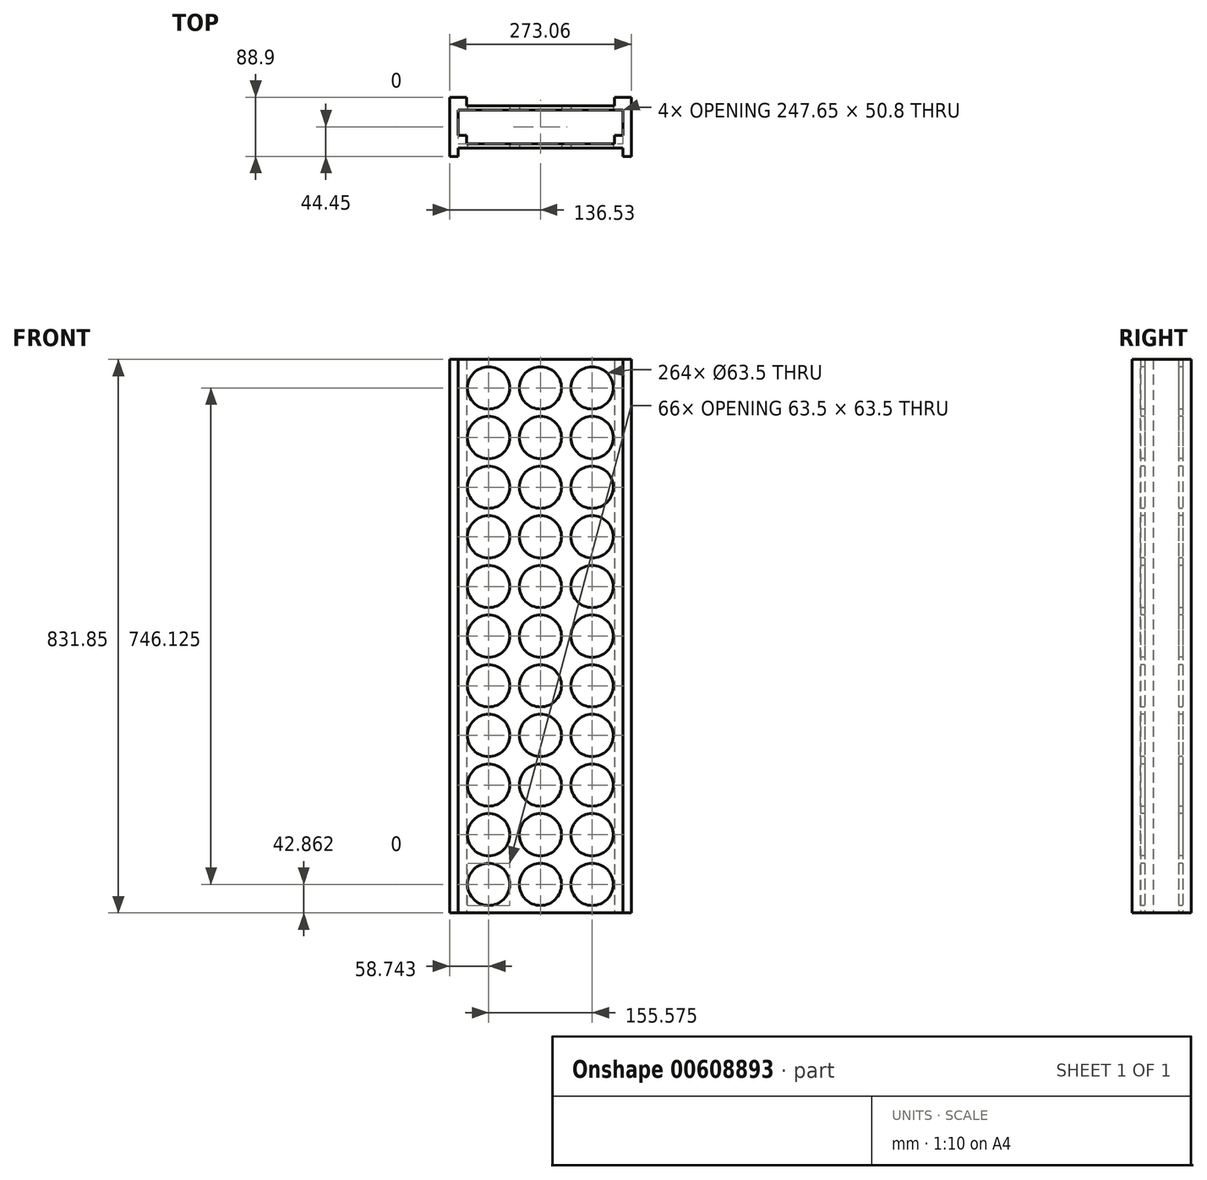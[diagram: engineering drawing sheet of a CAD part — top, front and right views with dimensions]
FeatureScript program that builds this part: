
annotation { "Feature Type Name" : "Feature", "Feature Type Description" : "" }
export const myFeature = defineFeature(function(context is Context, id is Id, definition is map)
    precondition{}
    {
        {
            var Q0;
            Q0=qCreatedBy(makeId("Top.planeOp"),FACE);
            var sketch = newSketch(context, id + "F0", { "sketchPlane" : qUnion([Q0])});
            skLineSegment(sketch, "E0", {"start": v(0, 0) * mm, "end": v(136.52, 0) * mm, "construction": true});
            skLineSegment(sketch, "E1", {"start": v(0, 0) * mm, "end": v(-136.53, 0) * mm, "construction": true});
            skLineSegment(sketch, "E2", {"start": v(-136.53, 0) * mm, "end": v(-136.53, 44.45) * mm, "construction": true});
            skLineSegment(sketch, "E3", {"start": v(-136.53, 0) * mm, "end": v(-136.53, -44.45) * mm, "construction": true});
            skLineSegment(sketch, "E4", {"start": v(136.52, 0) * mm, "end": v(136.52, 44.45) * mm, "construction": true});
            skLineSegment(sketch, "E5", {"start": v(136.52, 0) * mm, "end": v(136.52, -44.45) * mm, "construction": true});
            skLineSegment(sketch, "E6.bottom", {"start": v(-136.53, 44.45) * mm, "end": v(-123.83, 44.45) * mm});
            skLineSegment(sketch, "E6.top", {"start": v(-136.53, -44.45) * mm, "end": v(-123.83, -44.45) * mm});
            skLineSegment(sketch, "E6.left", {"start": v(-136.53, 44.45) * mm, "end": v(-136.53, -44.45) * mm});
            skLineSegment(sketch, "E6.right", {"start": v(-123.83, 44.45) * mm, "end": v(-123.83, -44.45) * mm});
            skLineSegment(sketch, "E7.bottom", {"start": v(136.52, 44.45) * mm, "end": v(123.82, 44.45) * mm});
            skLineSegment(sketch, "E7.top", {"start": v(136.52, -44.45) * mm, "end": v(123.83, -44.45) * mm});
            skLineSegment(sketch, "E7.left", {"start": v(136.52, 44.45) * mm, "end": v(136.52, -44.45) * mm});
            skLineSegment(sketch, "E7.right", {"start": v(123.82, 44.45) * mm, "end": v(123.83, -44.45) * mm});
            skLineSegment(sketch, "E8", {"start": v(-123.83, -44.45) * mm, "end": v(-123.83, -31.75) * mm, "construction": true});
            skLineSegment(sketch, "E9.left", {"start": v(-123.83, -31.75) * mm, "end": v(-123.83, -25.4) * mm});
            skLineSegment(sketch, "E9.right", {"start": v(123.83, -31.75) * mm, "end": v(123.83, -25.4) * mm});
            skLineSegment(sketch, "E10.bottom", {"start": v(-123.83, -31.75) * mm, "end": v(123.83, -31.75) * mm});
            skLineSegment(sketch, "E10.top", {"start": v(-123.83, -25.4) * mm, "end": v(123.83, -25.4) * mm});
            skLineSegment(sketch, "E11.bottom", {"start": v(-123.83, -25.4) * mm, "end": v(-111.12, -25.4) * mm});
            skLineSegment(sketch, "E11.top", {"start": v(-123.83, -12.7) * mm, "end": v(-111.12, -12.7) * mm});
            skLineSegment(sketch, "E11.left", {"start": v(-123.83, -25.4) * mm, "end": v(-123.83, -12.7) * mm});
            skLineSegment(sketch, "E11.right", {"start": v(-111.12, -25.4) * mm, "end": v(-111.12, -12.7) * mm});
            skLineSegment(sketch, "E12.bottom", {"start": v(123.83, -25.4) * mm, "end": v(111.12, -25.4) * mm});
            skLineSegment(sketch, "E12.top", {"start": v(123.83, -12.7) * mm, "end": v(111.12, -12.7) * mm});
            skLineSegment(sketch, "E12.left", {"start": v(123.83, -25.4) * mm, "end": v(123.83, -12.7) * mm});
            skLineSegment(sketch, "E12.right", {"start": v(111.12, -25.4) * mm, "end": v(111.12, -12.7) * mm});
            skLineSegment(sketch, "E13.bottom", {"start": v(-123.83, 44.45) * mm, "end": v(-111.12, 44.45) * mm});
            skLineSegment(sketch, "E13.top", {"start": v(-123.83, 31.75) * mm, "end": v(-111.12, 31.75) * mm});
            skLineSegment(sketch, "E13.left", {"start": v(-123.83, 44.45) * mm, "end": v(-123.83, 31.75) * mm});
            skLineSegment(sketch, "E13.right", {"start": v(-111.12, 44.45) * mm, "end": v(-111.12, 31.75) * mm});
            skLineSegment(sketch, "E14.bottom", {"start": v(123.82, 44.45) * mm, "end": v(111.12, 44.45) * mm});
            skLineSegment(sketch, "E14.top", {"start": v(123.82, 31.75) * mm, "end": v(111.12, 31.75) * mm});
            skLineSegment(sketch, "E14.left", {"start": v(123.82, 44.45) * mm, "end": v(123.82, 31.75) * mm});
            skLineSegment(sketch, "E14.right", {"start": v(111.12, 44.45) * mm, "end": v(111.12, 31.75) * mm});
            skLineSegment(sketch, "E15.bottom", {"start": v(-123.82, 31.75) * mm, "end": v(123.82, 31.75) * mm});
            skLineSegment(sketch, "E15.top", {"start": v(-123.82, 25.4) * mm, "end": v(123.82, 25.4) * mm});
            skLineSegment(sketch, "E15.left", {"start": v(-123.83, 31.75) * mm, "end": v(-123.83, 25.4) * mm});
            skLineSegment(sketch, "E15.right", {"start": v(123.82, 31.75) * mm, "end": v(123.82, 25.4) * mm});
            skSolve(sketch);
        }
        {
            var Q0;
            {var subQ4=sQuery(id+"F0.wireOp",EDGE,"E6.bottom");Q0=makeQuery(id+"F0.imprint","IMPRINT",FACE,{"disambiguationData":[TD([[makeQuery(id+"F0.imprint","IMPRINT",EDGE,{"derivedFrom":subQ4}),-1.0]])]});}
            var Q1;
            {var subQ0=sQuery(id+"F0.wireOp",EDGE,"E13.bottom");Q1=makeQuery(id+"F0.imprint","IMPRINT",FACE,{"disambiguationData":[TD([[makeQuery(id+"F0.imprint","IMPRINT",EDGE,{"derivedFrom":subQ0}),-1.0]])]});}
            var Q2;
            {var subQ3=sQuery(id+"F0.wireOp",EDGE,"E13.top");Q2=makeQuery(id+"F0.imprint","IMPRINT",FACE,{"disambiguationData":[TD([[makeQuery(id+"F0.imprint","IMPRINT",EDGE,{"derivedFrom":subQ3}),-1.0]])]});}
            var Q3;
            {var subQ0=sQuery(id+"F0.wireOp",EDGE,"E14.bottom");Q3=makeQuery(id+"F0.imprint","IMPRINT",FACE,{"disambiguationData":[TD([[makeQuery(id+"F0.imprint","IMPRINT",EDGE,{"derivedFrom":subQ0}),1.0]])]});}
            var Q4;
            {var subQ4=sQuery(id+"F0.wireOp",EDGE,"E7.bottom");Q4=makeQuery(id+"F0.imprint","IMPRINT",FACE,{"disambiguationData":[TD([[makeQuery(id+"F0.imprint","IMPRINT",EDGE,{"derivedFrom":subQ4}),1.0]])]});}
            var Q5;
            {var subQ0=sQuery(id+"F0.wireOp",EDGE,"E12.top");Q5=makeQuery(id+"F0.imprint","IMPRINT",FACE,{"disambiguationData":[TD([[makeQuery(id+"F0.imprint","IMPRINT",EDGE,{"derivedFrom":subQ0}),1.0]])]});}
            var Q6;
            {var subQ0=sQuery(id+"F0.wireOp",EDGE,"E11.top");Q6=makeQuery(id+"F0.imprint","IMPRINT",FACE,{"disambiguationData":[TD([[makeQuery(id+"F0.imprint","IMPRINT",EDGE,{"derivedFrom":subQ0}),-1.0]])]});}
            var Q7;
            {var subQ3=sQuery(id+"F0.wireOp",EDGE,"E10.bottom");Q7=makeQuery(id+"F0.imprint","IMPRINT",FACE,{"disambiguationData":[TD([[makeQuery(id+"F0.imprint","IMPRINT",EDGE,{"derivedFrom":subQ3}),1.0]])]});}
            extrude(context, id + "F1", {"entities" : qUnion([Q0, Q1, Q2, Q3, Q4, Q5, Q6, Q7]), "depth" : 831.85 * mm, "offsetDistance" : 25.4 * mm});
        }
        {
            var Q0;
            Q0=makeQuery(id+"F1.opExtrude","SWEPT_FACE",FACE,{"disambiguationData":[OSD([sQuery(id+"F0.wireOp",EDGE,"E10.bottom")])]});
            var sketch = newSketch(context, id + "F2", { "sketchPlane" : qUnion([Q0])});
            skLineSegment(sketch, "E16", {"start": v(-123.83, 0) * mm, "end": v(-123.83, 42.86) * mm, "construction": true});
            skLineSegment(sketch, "E17", {"start": v(-123.83, 42.86) * mm, "end": v(-123.83, 117.48) * mm, "construction": true});
            skLineSegment(sketch, "E18", {"start": v(-123.83, 117.48) * mm, "end": v(-123.83, 192.09) * mm, "construction": true});
            skLineSegment(sketch, "E19", {"start": v(-123.83, 192.09) * mm, "end": v(-123.83, 266.7) * mm, "construction": true});
            skLineSegment(sketch, "E20", {"start": v(-123.83, 266.7) * mm, "end": v(-123.83, 341.31) * mm, "construction": true});
            skLineSegment(sketch, "E21", {"start": v(-123.83, 341.31) * mm, "end": v(-123.83, 415.93) * mm, "construction": true});
            skLineSegment(sketch, "E22", {"start": v(-123.83, 415.93) * mm, "end": v(-123.83, 490.54) * mm, "construction": true});
            skLineSegment(sketch, "E23", {"start": v(-123.83, 490.54) * mm, "end": v(-123.83, 565.15) * mm, "construction": true});
            skLineSegment(sketch, "E24", {"start": v(-123.83, 565.15) * mm, "end": v(-123.83, 639.76) * mm, "construction": true});
            skLineSegment(sketch, "E25", {"start": v(-123.83, 639.76) * mm, "end": v(-123.83, 714.38) * mm, "construction": true});
            skLineSegment(sketch, "E26", {"start": v(-123.83, 714.38) * mm, "end": v(-123.83, 788.99) * mm, "construction": true});
            skLineSegment(sketch, "E27", {"start": v(-123.83, 788.99) * mm, "end": v(123.83, 788.99) * mm, "construction": true});
            skLineSegment(sketch, "E28", {"start": v(-123.83, 714.38) * mm, "end": v(123.83, 714.38) * mm, "construction": true});
            skLineSegment(sketch, "E29", {"start": v(123.83, 714.38) * mm, "end": v(123.9, 718.52) * mm, "construction": true});
            skLineSegment(sketch, "E30", {"start": v(-123.83, 639.76) * mm, "end": v(123.83, 639.76) * mm, "construction": true});
            skLineSegment(sketch, "E31", {"start": v(-123.83, 565.15) * mm, "end": v(123.83, 565.15) * mm, "construction": true});
            skLineSegment(sketch, "E32", {"start": v(-123.83, 490.54) * mm, "end": v(123.83, 490.54) * mm, "construction": true});
            skLineSegment(sketch, "E33", {"start": v(-123.83, 415.93) * mm, "end": v(123.83, 415.93) * mm, "construction": true});
            skLineSegment(sketch, "E34", {"start": v(123.83, 415.93) * mm, "end": v(120.66, 422.9) * mm, "construction": true});
            skLineSegment(sketch, "E35", {"start": v(-123.83, 341.31) * mm, "end": v(123.83, 341.31) * mm, "construction": true});
            skLineSegment(sketch, "E36", {"start": v(-123.83, 266.7) * mm, "end": v(123.83, 266.7) * mm, "construction": true});
            skLineSegment(sketch, "E37", {"start": v(-123.83, 192.09) * mm, "end": v(123.83, 192.09) * mm, "construction": true});
            skLineSegment(sketch, "E38", {"start": v(-123.83, 117.48) * mm, "end": v(123.83, 117.48) * mm, "construction": true});
            skLineSegment(sketch, "E39", {"start": v(-123.83, 42.86) * mm, "end": v(123.83, 42.86) * mm, "construction": true});
            skLineSegment(sketch, "E40", {"start": v(123.83, 0) * mm, "end": v(77.79, 0) * mm, "construction": true});
            skLineSegment(sketch, "E41", {"start": v(77.79, 0) * mm, "end": v(0, 0) * mm, "construction": true});
            skLineSegment(sketch, "E42", {"start": v(0, 0) * mm, "end": v(-77.79, 0) * mm, "construction": true});
            skLineSegment(sketch, "E43", {"start": v(-77.79, 0) * mm, "end": v(-77.79, 831.85) * mm, "construction": true});
            skLineSegment(sketch, "E44", {"start": v(0, 0) * mm, "end": v(0, 831.85) * mm, "construction": true});
            skLineSegment(sketch, "E45", {"start": v(77.79, 0) * mm, "end": v(77.79, 831.85) * mm, "construction": true});
            skLineSegment(sketch, "E46", {"start": v(77.79, 831.85) * mm, "end": v(76.8, 837.1) * mm, "construction": true});
            skCircle(sketch, "E47", {"center": v(-77.79, 42.86) * mm, "radius": 31.75 * mm});
            skCircle(sketch, "E48", {"center": v(-77.79, 117.48) * mm, "radius": 31.75 * mm});
            skCircle(sketch, "E49", {"center": v(-77.79, 192.09) * mm, "radius": 31.75 * mm});
            skCircle(sketch, "E50", {"center": v(-77.79, 266.7) * mm, "radius": 31.75 * mm});
            skCircle(sketch, "E51", {"center": v(0, 266.7) * mm, "radius": 31.75 * mm});
            skCircle(sketch, "E52", {"center": v(0, 192.09) * mm, "radius": 31.75 * mm});
            skCircle(sketch, "E53", {"center": v(0, 117.48) * mm, "radius": 31.75 * mm});
            skCircle(sketch, "E54", {"center": v(0, 42.86) * mm, "radius": 31.75 * mm});
            skCircle(sketch, "E55", {"center": v(77.79, 42.86) * mm, "radius": 31.75 * mm});
            skCircle(sketch, "E56", {"center": v(77.79, 117.48) * mm, "radius": 31.75 * mm});
            skCircle(sketch, "E57", {"center": v(77.79, 192.09) * mm, "radius": 31.75 * mm});
            skCircle(sketch, "E58", {"center": v(77.79, 266.7) * mm, "radius": 31.75 * mm});
            skCircle(sketch, "E59", {"center": v(-77.79, 341.31) * mm, "radius": 31.75 * mm});
            skCircle(sketch, "E60", {"center": v(-77.79, 415.93) * mm, "radius": 31.75 * mm});
            skCircle(sketch, "E61", {"center": v(-77.79, 490.54) * mm, "radius": 31.75 * mm});
            skCircle(sketch, "E62", {"center": v(-77.79, 565.15) * mm, "radius": 31.75 * mm});
            skCircle(sketch, "E63", {"center": v(-77.79, 639.76) * mm, "radius": 31.75 * mm});
            skCircle(sketch, "E64", {"center": v(-77.79, 714.38) * mm, "radius": 31.75 * mm});
            skCircle(sketch, "E65", {"center": v(-77.79, 788.99) * mm, "radius": 31.75 * mm});
            skCircle(sketch, "E66", {"center": v(0, 788.99) * mm, "radius": 31.75 * mm});
            skCircle(sketch, "E67", {"center": v(0, 714.38) * mm, "radius": 31.75 * mm});
            skCircle(sketch, "E68", {"center": v(0, 639.76) * mm, "radius": 31.75 * mm});
            skCircle(sketch, "E69", {"center": v(0, 565.15) * mm, "radius": 31.75 * mm});
            skCircle(sketch, "E70", {"center": v(0, 490.54) * mm, "radius": 31.75 * mm});
            skCircle(sketch, "E71", {"center": v(0, 415.93) * mm, "radius": 31.75 * mm});
            skCircle(sketch, "E72", {"center": v(0, 341.31) * mm, "radius": 31.75 * mm});
            skCircle(sketch, "E73", {"center": v(77.79, 788.99) * mm, "radius": 31.75 * mm});
            skCircle(sketch, "E74", {"center": v(77.79, 714.38) * mm, "radius": 31.75 * mm});
            skCircle(sketch, "E75", {"center": v(77.79, 639.76) * mm, "radius": 31.75 * mm});
            skCircle(sketch, "E76", {"center": v(77.79, 565.15) * mm, "radius": 31.75 * mm});
            skCircle(sketch, "E77", {"center": v(77.79, 490.54) * mm, "radius": 31.75 * mm});
            skCircle(sketch, "E78", {"center": v(77.79, 415.93) * mm, "radius": 31.75 * mm});
            skCircle(sketch, "E79", {"center": v(77.79, 341.31) * mm, "radius": 31.75 * mm});
            skSolve(sketch);
        }
        {
            var Q0;
            Q0=makeQuery(id+"F2.imprint","IMPRINT",FACE,{"disambiguationData":[TD([[makeQuery(id+"F2.imprint","IMPRINT",EDGE,{"derivedFrom":sQuery(id+"F2.wireOp",EDGE,"E65")}),1.0]])]});
            var Q1;
            Q1=makeQuery(id+"F2.imprint","IMPRINT",FACE,{"disambiguationData":[TD([[makeQuery(id+"F2.imprint","IMPRINT",EDGE,{"derivedFrom":sQuery(id+"F2.wireOp",EDGE,"E66")}),1.0]])]});
            var Q2;
            Q2=makeQuery(id+"F2.imprint","IMPRINT",FACE,{"disambiguationData":[TD([[makeQuery(id+"F2.imprint","IMPRINT",EDGE,{"derivedFrom":sQuery(id+"F2.wireOp",EDGE,"E73")}),1.0]])]});
            var Q3;
            Q3=makeQuery(id+"F2.imprint","IMPRINT",FACE,{"disambiguationData":[TD([[makeQuery(id+"F2.imprint","IMPRINT",EDGE,{"derivedFrom":sQuery(id+"F2.wireOp",EDGE,"E74")}),1.0]])]});
            var Q4;
            Q4=makeQuery(id+"F2.imprint","IMPRINT",FACE,{"disambiguationData":[TD([[makeQuery(id+"F2.imprint","IMPRINT",EDGE,{"derivedFrom":sQuery(id+"F2.wireOp",EDGE,"E67")}),1.0]])]});
            var Q5;
            Q5=makeQuery(id+"F2.imprint","IMPRINT",FACE,{"disambiguationData":[TD([[makeQuery(id+"F2.imprint","IMPRINT",EDGE,{"derivedFrom":sQuery(id+"F2.wireOp",EDGE,"E64")}),1.0]])]});
            var Q6;
            Q6=makeQuery(id+"F2.imprint","IMPRINT",FACE,{"disambiguationData":[TD([[makeQuery(id+"F2.imprint","IMPRINT",EDGE,{"derivedFrom":sQuery(id+"F2.wireOp",EDGE,"E63")}),1.0]])]});
            var Q7;
            Q7=makeQuery(id+"F2.imprint","IMPRINT",FACE,{"disambiguationData":[TD([[makeQuery(id+"F2.imprint","IMPRINT",EDGE,{"derivedFrom":sQuery(id+"F2.wireOp",EDGE,"E68")}),1.0]])]});
            var Q8;
            Q8=makeQuery(id+"F2.imprint","IMPRINT",FACE,{"disambiguationData":[TD([[makeQuery(id+"F2.imprint","IMPRINT",EDGE,{"derivedFrom":sQuery(id+"F2.wireOp",EDGE,"E75")}),1.0]])]});
            var Q9;
            Q9=makeQuery(id+"F2.imprint","IMPRINT",FACE,{"disambiguationData":[TD([[makeQuery(id+"F2.imprint","IMPRINT",EDGE,{"derivedFrom":sQuery(id+"F2.wireOp",EDGE,"E76")}),1.0]])]});
            var Q10;
            Q10=makeQuery(id+"F2.imprint","IMPRINT",FACE,{"disambiguationData":[TD([[makeQuery(id+"F2.imprint","IMPRINT",EDGE,{"derivedFrom":sQuery(id+"F2.wireOp",EDGE,"E69")}),1.0]])]});
            var Q11;
            Q11=makeQuery(id+"F2.imprint","IMPRINT",FACE,{"disambiguationData":[TD([[makeQuery(id+"F2.imprint","IMPRINT",EDGE,{"derivedFrom":sQuery(id+"F2.wireOp",EDGE,"E62")}),1.0]])]});
            var Q12;
            Q12=makeQuery(id+"F2.imprint","IMPRINT",FACE,{"disambiguationData":[TD([[makeQuery(id+"F2.imprint","IMPRINT",EDGE,{"derivedFrom":sQuery(id+"F2.wireOp",EDGE,"E61")}),1.0]])]});
            var Q13;
            Q13=makeQuery(id+"F2.imprint","IMPRINT",FACE,{"disambiguationData":[TD([[makeQuery(id+"F2.imprint","IMPRINT",EDGE,{"derivedFrom":sQuery(id+"F2.wireOp",EDGE,"E70")}),1.0]])]});
            var Q14;
            Q14=makeQuery(id+"F2.imprint","IMPRINT",FACE,{"disambiguationData":[TD([[makeQuery(id+"F2.imprint","IMPRINT",EDGE,{"derivedFrom":sQuery(id+"F2.wireOp",EDGE,"E77")}),1.0]])]});
            var Q15;
            Q15=makeQuery(id+"F2.imprint","IMPRINT",FACE,{"disambiguationData":[TD([[makeQuery(id+"F2.imprint","IMPRINT",EDGE,{"derivedFrom":sQuery(id+"F2.wireOp",EDGE,"E78")}),1.0]])]});
            var Q16;
            Q16=makeQuery(id+"F2.imprint","IMPRINT",FACE,{"disambiguationData":[TD([[makeQuery(id+"F2.imprint","IMPRINT",EDGE,{"derivedFrom":sQuery(id+"F2.wireOp",EDGE,"E71")}),1.0]])]});
            var Q17;
            Q17=makeQuery(id+"F2.imprint","IMPRINT",FACE,{"disambiguationData":[TD([[makeQuery(id+"F2.imprint","IMPRINT",EDGE,{"derivedFrom":sQuery(id+"F2.wireOp",EDGE,"E60")}),1.0]])]});
            var Q18;
            Q18=makeQuery(id+"F2.imprint","IMPRINT",FACE,{"disambiguationData":[TD([[makeQuery(id+"F2.imprint","IMPRINT",EDGE,{"derivedFrom":sQuery(id+"F2.wireOp",EDGE,"E72")}),1.0]])]});
            var Q19;
            Q19=makeQuery(id+"F2.imprint","IMPRINT",FACE,{"disambiguationData":[TD([[makeQuery(id+"F2.imprint","IMPRINT",EDGE,{"derivedFrom":sQuery(id+"F2.wireOp",EDGE,"E79")}),1.0]])]});
            var Q20;
            Q20=makeQuery(id+"F2.imprint","IMPRINT",FACE,{"disambiguationData":[TD([[makeQuery(id+"F2.imprint","IMPRINT",EDGE,{"derivedFrom":sQuery(id+"F2.wireOp",EDGE,"E58")}),1.0]])]});
            var Q21;
            Q21=makeQuery(id+"F2.imprint","IMPRINT",FACE,{"disambiguationData":[TD([[makeQuery(id+"F2.imprint","IMPRINT",EDGE,{"derivedFrom":sQuery(id+"F2.wireOp",EDGE,"E51")}),1.0]])]});
            var Q22;
            Q22=makeQuery(id+"F2.imprint","IMPRINT",FACE,{"disambiguationData":[TD([[makeQuery(id+"F2.imprint","IMPRINT",EDGE,{"derivedFrom":sQuery(id+"F2.wireOp",EDGE,"E50")}),1.0]])]});
            var Q23;
            Q23=makeQuery(id+"F2.imprint","IMPRINT",FACE,{"disambiguationData":[TD([[makeQuery(id+"F2.imprint","IMPRINT",EDGE,{"derivedFrom":sQuery(id+"F2.wireOp",EDGE,"E59")}),1.0]])]});
            var Q24;
            Q24=makeQuery(id+"F2.imprint","IMPRINT",FACE,{"disambiguationData":[TD([[makeQuery(id+"F2.imprint","IMPRINT",EDGE,{"derivedFrom":sQuery(id+"F2.wireOp",EDGE,"E49")}),1.0]])]});
            var Q25;
            Q25=makeQuery(id+"F2.imprint","IMPRINT",FACE,{"disambiguationData":[TD([[makeQuery(id+"F2.imprint","IMPRINT",EDGE,{"derivedFrom":sQuery(id+"F2.wireOp",EDGE,"E52")}),1.0]])]});
            var Q26;
            Q26=makeQuery(id+"F2.imprint","IMPRINT",FACE,{"disambiguationData":[TD([[makeQuery(id+"F2.imprint","IMPRINT",EDGE,{"derivedFrom":sQuery(id+"F2.wireOp",EDGE,"E57")}),1.0]])]});
            var Q27;
            Q27=makeQuery(id+"F2.imprint","IMPRINT",FACE,{"disambiguationData":[TD([[makeQuery(id+"F2.imprint","IMPRINT",EDGE,{"derivedFrom":sQuery(id+"F2.wireOp",EDGE,"E56")}),1.0]])]});
            var Q28;
            Q28=makeQuery(id+"F2.imprint","IMPRINT",FACE,{"disambiguationData":[TD([[makeQuery(id+"F2.imprint","IMPRINT",EDGE,{"derivedFrom":sQuery(id+"F2.wireOp",EDGE,"E53")}),1.0]])]});
            var Q29;
            Q29=makeQuery(id+"F2.imprint","IMPRINT",FACE,{"disambiguationData":[TD([[makeQuery(id+"F2.imprint","IMPRINT",EDGE,{"derivedFrom":sQuery(id+"F2.wireOp",EDGE,"E48")}),1.0]])]});
            var Q30;
            Q30=makeQuery(id+"F2.imprint","IMPRINT",FACE,{"disambiguationData":[TD([[makeQuery(id+"F2.imprint","IMPRINT",EDGE,{"derivedFrom":sQuery(id+"F2.wireOp",EDGE,"E47")}),1.0]])]});
            var Q31;
            Q31=makeQuery(id+"F2.imprint","IMPRINT",FACE,{"disambiguationData":[TD([[makeQuery(id+"F2.imprint","IMPRINT",EDGE,{"derivedFrom":sQuery(id+"F2.wireOp",EDGE,"E54")}),1.0]])]});
            var Q32;
            Q32=makeQuery(id+"F2.imprint","IMPRINT",FACE,{"disambiguationData":[TD([[makeQuery(id+"F2.imprint","IMPRINT",EDGE,{"derivedFrom":sQuery(id+"F2.wireOp",EDGE,"E55")}),1.0]])]});
            extrude(context, id + "F3", {"entities" : qUnion([Q0, Q1, Q2, Q3, Q4, Q5, Q6, Q7, Q8, Q9, Q10, Q11, Q12, Q13, Q14, Q15, Q16, Q17, Q18, Q19, Q20, Q21, Q22, Q23, Q24, Q25, Q26, Q27, Q28, Q29, Q30, Q31, Q32]), "operationType" : NewBodyOperationType.REMOVE, "endBound" : BoundingType.THROUGH_ALL, "oppositeDirection" : true, "depth" : 25.4 * mm, "offsetDistance" : 25.4 * mm});
        }
    });
